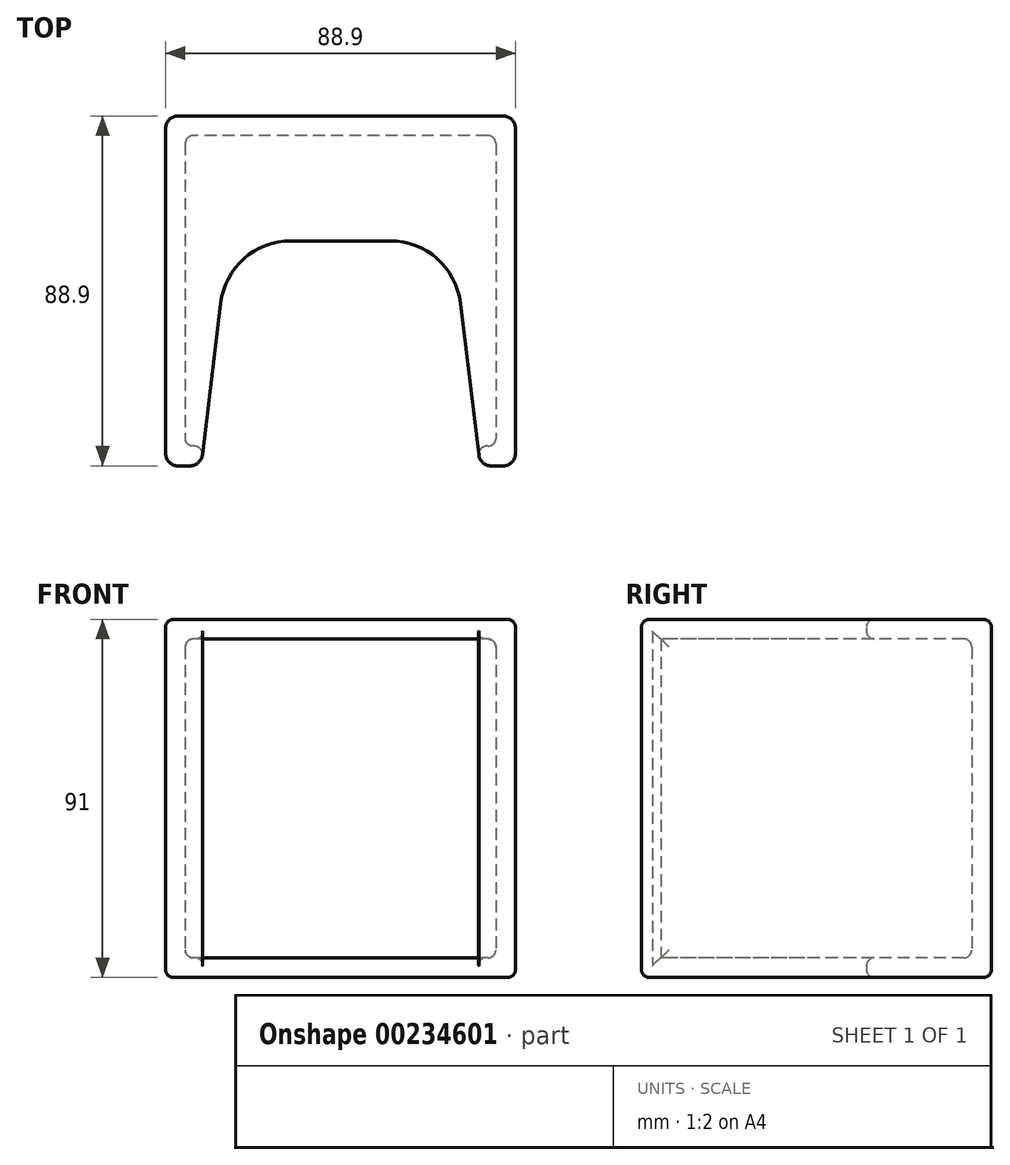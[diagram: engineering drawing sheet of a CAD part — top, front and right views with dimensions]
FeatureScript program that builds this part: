
annotation { "Feature Type Name" : "Feature", "Feature Type Description" : "" }
export const myFeature = defineFeature(function(context is Context, id is Id, definition is map)
    precondition{}
    {
        {
            var Q0;
            Q0=qCreatedBy(makeId("Top.planeOp"),FACE);
            var sketch = newSketch(context, id + "F0", { "sketchPlane" : qUnion([Q0])});
            skLineSegment(sketch, "E0.bottom", {"start": v(41.27, 44.45) * mm, "end": v(-41.28, 44.45) * mm});
            skLineSegment(sketch, "E0.top", {"start": v(41.28, -44.45) * mm, "end": v(38.27, -44.45) * mm});
            skLineSegment(sketch, "E0.left", {"start": v(44.45, 41.28) * mm, "end": v(44.45, -41.28) * mm});
            skLineSegment(sketch, "E0.right", {"start": v(-44.45, 41.27) * mm, "end": v(-44.45, -41.28) * mm});
            skPoint(sketch, "E0.middle", {"position": v(0, 0) * mm});
            skLineSegment(sketch, "E1", {"start": v(35.11, -41.65) * mm, "end": v(30.48, -3.15) * mm});
            skLineSegment(sketch, "E2", {"start": v(12.61, 12.7) * mm, "end": v(-12.61, 12.7) * mm});
            skLineSegment(sketch, "E3", {"start": v(-30.48, -3.15) * mm, "end": v(-35.11, -41.65) * mm});
            skPoint(sketch, "E4.visualSharp", {"position": v(-28.58, 12.7) * mm});
            skArc(sketch, "E4.filletArc", {"start": v(-12.61, 12.7) * mm, "mid": v(-24.55, 8.17) * mm, "end": v(-30.48, -3.15) * mm});
            skPoint(sketch, "E5.visualSharp", {"position": v(28.58, 12.7) * mm});
            skArc(sketch, "E5.filletArc", {"start": v(30.48, -3.15) * mm, "mid": v(24.55, 8.17) * mm, "end": v(12.61, 12.7) * mm});
            skLineSegment(sketch, "E6.trimOffspring", {"start": v(-38.27, -44.45) * mm, "end": v(-41.28, -44.45) * mm});
            skPoint(sketch, "E7.visualSharp", {"position": v(-35.45, -44.45) * mm});
            skArc(sketch, "E7.filletArc", {"start": v(-38.27, -44.45) * mm, "mid": v(-36.16, -43.65) * mm, "end": v(-35.11, -41.65) * mm});
            skPoint(sketch, "E8.visualSharp", {"position": v(-44.45, -44.45) * mm});
            skArc(sketch, "E8.filletArc", {"start": v(-44.45, -41.28) * mm, "mid": v(-43.52, -43.52) * mm, "end": v(-41.28, -44.45) * mm});
            skPoint(sketch, "E9.visualSharp", {"position": v(35.45, -44.45) * mm});
            skArc(sketch, "E9.filletArc", {"start": v(35.11, -41.65) * mm, "mid": v(36.16, -43.65) * mm, "end": v(38.27, -44.45) * mm});
            skPoint(sketch, "E10.visualSharp", {"position": v(44.45, -44.45) * mm});
            skArc(sketch, "E10.filletArc", {"start": v(41.28, -44.45) * mm, "mid": v(43.52, -43.52) * mm, "end": v(44.45, -41.28) * mm});
            skPoint(sketch, "E11.visualSharp", {"position": v(-44.45, 44.45) * mm});
            skArc(sketch, "E11.filletArc", {"start": v(-41.28, 44.45) * mm, "mid": v(-43.52, 43.52) * mm, "end": v(-44.45, 41.27) * mm});
            skPoint(sketch, "E12.visualSharp", {"position": v(44.45, 44.45) * mm});
            skArc(sketch, "E12.filletArc", {"start": v(44.45, 41.28) * mm, "mid": v(43.52, 43.52) * mm, "end": v(41.27, 44.45) * mm});
            skSolve(sketch);
        }
        {
            var Q0;
            Q0=makeQuery(id+"F0.imprint","IMPRINT",FACE,{"disambiguationData":[TD([[makeQuery(id+"F0.imprint","IMPRINT",EDGE,{"derivedFrom":sQuery(id+"F0.wireOp",EDGE,"E0.bottom")}),1.0]])]});
            extrude(context, id + "F1", {"entities" : qUnion([Q0]), "depth" : 91 * mm});
        }
        {
            var Q0;
            Q0=makeQuery(id+"F1.opExtrude","SWEPT_FACE",FACE,{"disambiguationData":[OSD([sQuery(id+"F0.wireOp",EDGE,"E2")])]});
            var Q1;
            Q1=makeQuery(id+"F1.opExtrude","SWEPT_FACE",FACE,{"disambiguationData":[OSD([sQuery(id+"F0.wireOp",EDGE,"E4.filletArc")])]});
            var Q2;
            Q2=makeQuery(id+"F1.opExtrude","SWEPT_FACE",FACE,{"disambiguationData":[OSD([sQuery(id+"F0.wireOp",EDGE,"E5.filletArc")])]});
            var Q3;
            Q3=makeQuery(id+"F1.opExtrude","SWEPT_FACE",FACE,{"disambiguationData":[OSD([sQuery(id+"F0.wireOp",EDGE,"E1")])]});
            var Q4;
            Q4=makeQuery(id+"F1.opExtrude","SWEPT_FACE",FACE,{"disambiguationData":[OSD([sQuery(id+"F0.wireOp",EDGE,"E3")])]});
            shell(context, id + "F2", {"entities" : qUnion([Q0, Q1, Q2, Q3, Q4]), "thickness" : 5 * mm});
        }
        {
            var Q0;
            Q0=makeQuery(id+"F1.opExtrude","CAP_FACE",FACE,{"disambiguationData":[OSD([sQuery(id+"F0.wireOp",EDGE,"E0.bottom"),sQuery(id+"F0.wireOp",EDGE,"E0.top"),sQuery(id+"F0.wireOp",EDGE,"E0.left"),sQuery(id+"F0.wireOp",EDGE,"E0.right"),sQuery(id+"F0.wireOp",EDGE,"E1"),sQuery(id+"F0.wireOp",EDGE,"E2"),sQuery(id+"F0.wireOp",EDGE,"E3"),sQuery(id+"F0.wireOp",EDGE,"E4.filletArc"),sQuery(id+"F0.wireOp",EDGE,"E5.filletArc"),sQuery(id+"F0.wireOp",EDGE,"E6.trimOffspring"),sQuery(id+"F0.wireOp",EDGE,"E7.filletArc"),sQuery(id+"F0.wireOp",EDGE,"E8.filletArc"),sQuery(id+"F0.wireOp",EDGE,"E9.filletArc"),sQuery(id+"F0.wireOp",EDGE,"E10.filletArc"),sQuery(id+"F0.wireOp",EDGE,"E11.filletArc"),sQuery(id+"F0.wireOp",EDGE,"E12.filletArc")])],"isStart":false});
            var Q1;
            Q1=makeQuery(id+"F1.opExtrude","CAP_FACE",FACE,{"disambiguationData":[OSD([sQuery(id+"F0.wireOp",EDGE,"E0.bottom"),sQuery(id+"F0.wireOp",EDGE,"E0.top"),sQuery(id+"F0.wireOp",EDGE,"E0.left"),sQuery(id+"F0.wireOp",EDGE,"E0.right"),sQuery(id+"F0.wireOp",EDGE,"E1"),sQuery(id+"F0.wireOp",EDGE,"E2"),sQuery(id+"F0.wireOp",EDGE,"E3"),sQuery(id+"F0.wireOp",EDGE,"E4.filletArc"),sQuery(id+"F0.wireOp",EDGE,"E5.filletArc"),sQuery(id+"F0.wireOp",EDGE,"E6.trimOffspring"),sQuery(id+"F0.wireOp",EDGE,"E7.filletArc"),sQuery(id+"F0.wireOp",EDGE,"E8.filletArc"),sQuery(id+"F0.wireOp",EDGE,"E9.filletArc"),sQuery(id+"F0.wireOp",EDGE,"E10.filletArc"),sQuery(id+"F0.wireOp",EDGE,"E11.filletArc"),sQuery(id+"F0.wireOp",EDGE,"E12.filletArc")])],"isStart":true});
            fillet(context, id + "F3", {"entities" : qUnion([Q0, Q1]), "radius" : 2 * mm, "tangentPropagation" : true, "allowEdgeOverflow" : false});
        }
        {
            var Q0;
            Q0=makeQuery(id+"F2.opShell","OFFSET_FACE",FACE,{"disambiguationData":[OSD([sQuery(id+"F0.wireOp",EDGE,"E0.left")])]});
            var Q1;
            Q1=makeQuery(id+"F1.opExtrude","SWEPT_FACE",FACE,{"disambiguationData":[OSD([sQuery(id+"F0.wireOp",EDGE,"E1")])]});
            var Q2;
            Q2=makeQuery(id+"F2.opShell","OFFSET_FACE",FACE,{"disambiguationData":[OSD([sQuery(id+"F0.wireOp",EDGE,"E0.right")])]});
            var Q3;
            Q3=makeQuery(id+"F1.opExtrude","SWEPT_FACE",FACE,{"disambiguationData":[OSD([sQuery(id+"F0.wireOp",EDGE,"E3")])]});
            var Q4;
            Q4=makeQuery(id+"F2.opShell","OFFSET_FACE",FACE,{"disambiguationData":[OSD([sQuery(id+"F0.wireOp",EDGE,"E0.bottom")])]});
            var Q5;
            {var subQ0=sQuery(id+"F0.wireOp",EDGE,"E2");Q5=makeQuery(id+"F2.opShell","OFFSET_EDGE",EDGE,{"disambiguationData":[OSD([subQ0]),TDD([makeQuery(id+"F1.opExtrude","CAP_EDGE",EDGE,{"disambiguationData":[OSD([subQ0])],"isStart":false})])]});}
            fillet(context, id + "F4", {"entities" : qUnion([Q0, Q1, Q2, Q3, Q4, Q5]), "radius" : 2 * mm, "tangentPropagation" : true, "allowEdgeOverflow" : false});
        }
    });
